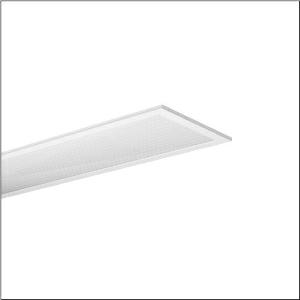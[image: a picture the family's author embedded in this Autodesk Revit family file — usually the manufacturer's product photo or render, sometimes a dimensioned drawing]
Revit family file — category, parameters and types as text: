
# Revit family: apollon_r__21_linear_51mq14wd2t12_0b39
name_source: partatom
category: Lighting Fixtures
units: mm (PartAtom-declared; Revit-internal decimal feet)

## family parameters
Cut with Voids When Loaded = No
Host = Face
Light Source = No
Part Type = Normal
Room Calculation Point = No
Round Connector Dimension = Use Diameter
Shared = No

## types (1)
- --- (1 x LED 2700 K ... 6500 K, 4200 lm, 44 W, 6500K)
    Apparent Load = 44 VA
    CIE Flux Codes = 60 87 97 100 100
    Color Rendering = 80
    Color Temperature = 6500K
    Default Elevation = 1800 mm
    Description = Apollon® 21 linear, office luminaire, primary optical cover: micro prismatic cover, of PMMA, CAT 2 (L<= 3000cd/m²), light emission: direct distribution, primary light characteristic: symmetric, installation type: lay-in mounting, LED, rated luminous flux: 4.200lm, luminous efficacy: 96lm/W, light colour: 8tw, colour temperature: 2700..6500K, with terminal, 5-pole, mains connection: 220..240V, AC, 50/60Hz, rated input power: 44W, housing, of aluminium, coated, pure white, length: 1.245mm, width: 307mm, height: 30mm, housing upper side, of sheet steel, galvanised, protection rating (complete): IP20, protection rating (lamp compartment, on room side): IP50, insulation class (complete): insulation class I (protective earthing), certification: CE, ENEC, packaging unit: 1 piece
    Height = 0 mm  [stored 0 ft]
    Lamp = 1 x LED 2700 K ... 6500 K
    Lamp Light Flux = 4200 lm
    Lamp Power = 44 W
    Lamp count = 1
    Length = 1245 mm
    Luminous efficacy = 95 lm/W
    Manufacturer = Siteco
    ModVariant = No
    Model = 51MQ14WD2T12
    Mounting Place = Ceiling
    Mounting Type = Recessed
    Number of Poles = 1
    OnlyDefault = Yes
    Power Factor = 1
    Product Name = Apollon® 21 linear
    Product group = office luminaire | ceiling recessed
    ProductGroupID = 401
    Protection Class = Protection class I
    Protection Degree = IP 20
    RLX_Detail_Level = 1
    RLX_Emergency_Light_Flux = 0 lm
    RLX_Emergency_Type = 0
    RLX_Emergency_Type_DB = No
    RlxData = <blob elided: 17565 chars, md5=7c354995>
    Socket = socket
    Standby Power = 0 W
    System Light Flux = 4200 lm
    System Power = 44 W
    Type Comments = individual setting: CCT=6500K, colour temperature 6500K
    Type Image = l_1291045.jpg
    URL = http://relux.com
    VarID = @adj_135359
    Voltage = 0 V
    Weight = 0.00 kg
    Width = 307 mm

note: [stored X ft] marks values corroborated as IEEE doubles in the binary element streams (Revit-internal decimal feet)

## geometry (parser evidence)
native form markers: Blend x4, Sweep x10
no freeform markers — native parametric forms only
